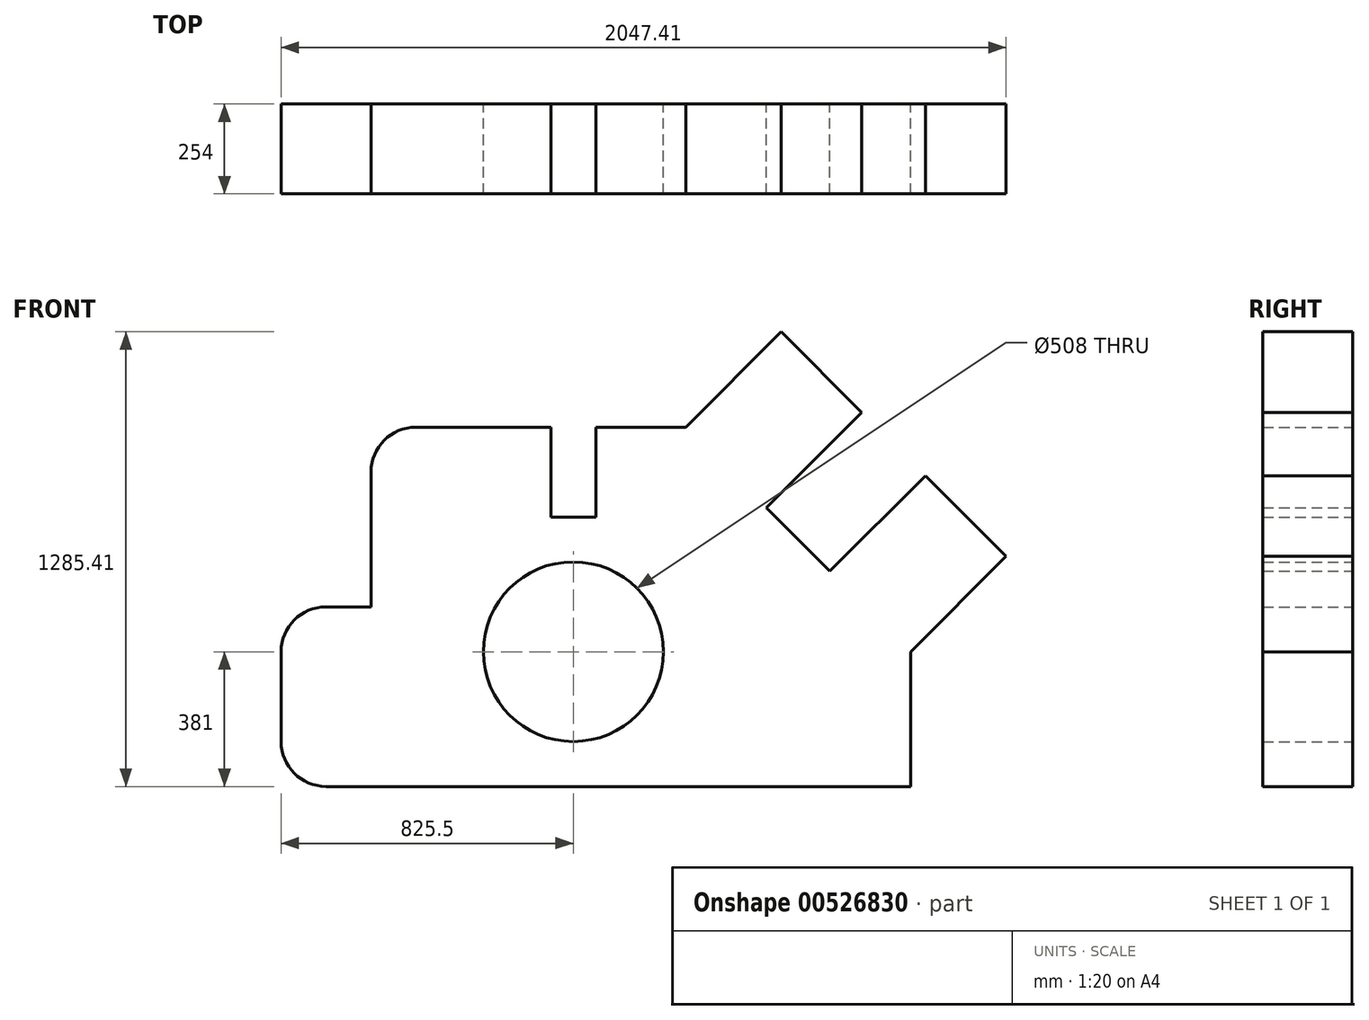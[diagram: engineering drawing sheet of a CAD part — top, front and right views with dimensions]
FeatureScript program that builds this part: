
annotation { "Feature Type Name" : "Feature", "Feature Type Description" : "" }
export const myFeature = defineFeature(function(context is Context, id is Id, definition is map)
    precondition{}
    {
        {
            var Q0;
            Q0=qCreatedBy(makeId("Front.planeOp"),FACE);
            var sketch = newSketch(context, id + "F0", { "sketchPlane" : qUnion([Q0])});
            skLineSegment(sketch, "E0", {"start": v(127, 0) * mm, "end": v(1778, 0) * mm});
            skLineSegment(sketch, "E1", {"start": v(1778, 0) * mm, "end": v(1778, 381) * mm});
            skLineSegment(sketch, "E2", {"start": v(0, 127) * mm, "end": v(0, 381) * mm});
            skPoint(sketch, "E3.visualSharp", {"position": v(0, 0) * mm});
            skArc(sketch, "E3.filletArc", {"start": v(0, 127) * mm, "mid": v(37.2, 37.2) * mm, "end": v(127, 0) * mm});
            skCircle(sketch, "E4", {"center": v(825.5, 381) * mm, "radius": 254 * mm});
            skLineSegment(sketch, "E5", {"start": v(127, 508) * mm, "end": v(254, 508) * mm});
            skLineSegment(sketch, "E6", {"start": v(254, 508) * mm, "end": v(254, 889) * mm});
            skLineSegment(sketch, "E7", {"start": v(381, 1016) * mm, "end": v(762, 1016) * mm});
            skLineSegment(sketch, "E8", {"start": v(762, 1016) * mm, "end": v(762, 762) * mm});
            skLineSegment(sketch, "E9", {"start": v(762, 762) * mm, "end": v(889, 762) * mm});
            skLineSegment(sketch, "E10", {"start": v(889, 762) * mm, "end": v(889, 1016) * mm});
            skLineSegment(sketch, "E11", {"start": v(889, 1016) * mm, "end": v(1143, 1016) * mm});
            skLineSegment(sketch, "E12", {"start": v(1778, 381) * mm, "end": v(2047.4, 650.4) * mm});
            skLineSegment(sketch, "E13", {"start": v(2047.4, 650.4) * mm, "end": v(1819.71, 878.1) * mm});
            skLineSegment(sketch, "E14", {"start": v(1819.71, 878.1) * mm, "end": v(1550.3, 608.7) * mm});
            skLineSegment(sketch, "E15", {"start": v(1550.3, 608.7) * mm, "end": v(1370.7, 788.3) * mm});
            skLineSegment(sketch, "E16", {"start": v(1370.7, 788.3) * mm, "end": v(1640.1, 1057.71) * mm});
            skLineSegment(sketch, "E17", {"start": v(1640.1, 1057.71) * mm, "end": v(1412.4, 1285.4) * mm});
            skLineSegment(sketch, "E18", {"start": v(1412.4, 1285.4) * mm, "end": v(1143, 1016) * mm});
            skPoint(sketch, "E19.visualSharp", {"position": v(254, 1016) * mm});
            skArc(sketch, "E19.filletArc", {"start": v(381, 1016) * mm, "mid": v(291.2, 978.8) * mm, "end": v(254, 889) * mm});
            skPoint(sketch, "E20.visualSharp", {"position": v(0, 508) * mm});
            skArc(sketch, "E20.filletArc", {"start": v(127, 508) * mm, "mid": v(37.2, 470.8) * mm, "end": v(0, 381) * mm});
            skSolve(sketch);
        }
        {
            var Q0;
            Q0=makeQuery(id+"F0.imprint","IMPRINT",FACE,{"disambiguationData":[TD([[makeQuery(id+"F0.imprint","IMPRINT",EDGE,{"derivedFrom":sQuery(id+"F0.wireOp",EDGE,"E0")}),1.0]])]});
            extrude(context, id + "F1", {"entities" : qUnion([Q0]), "depth" : 254 * mm, "offsetDistance" : 25.4 * mm});
        }
    });
